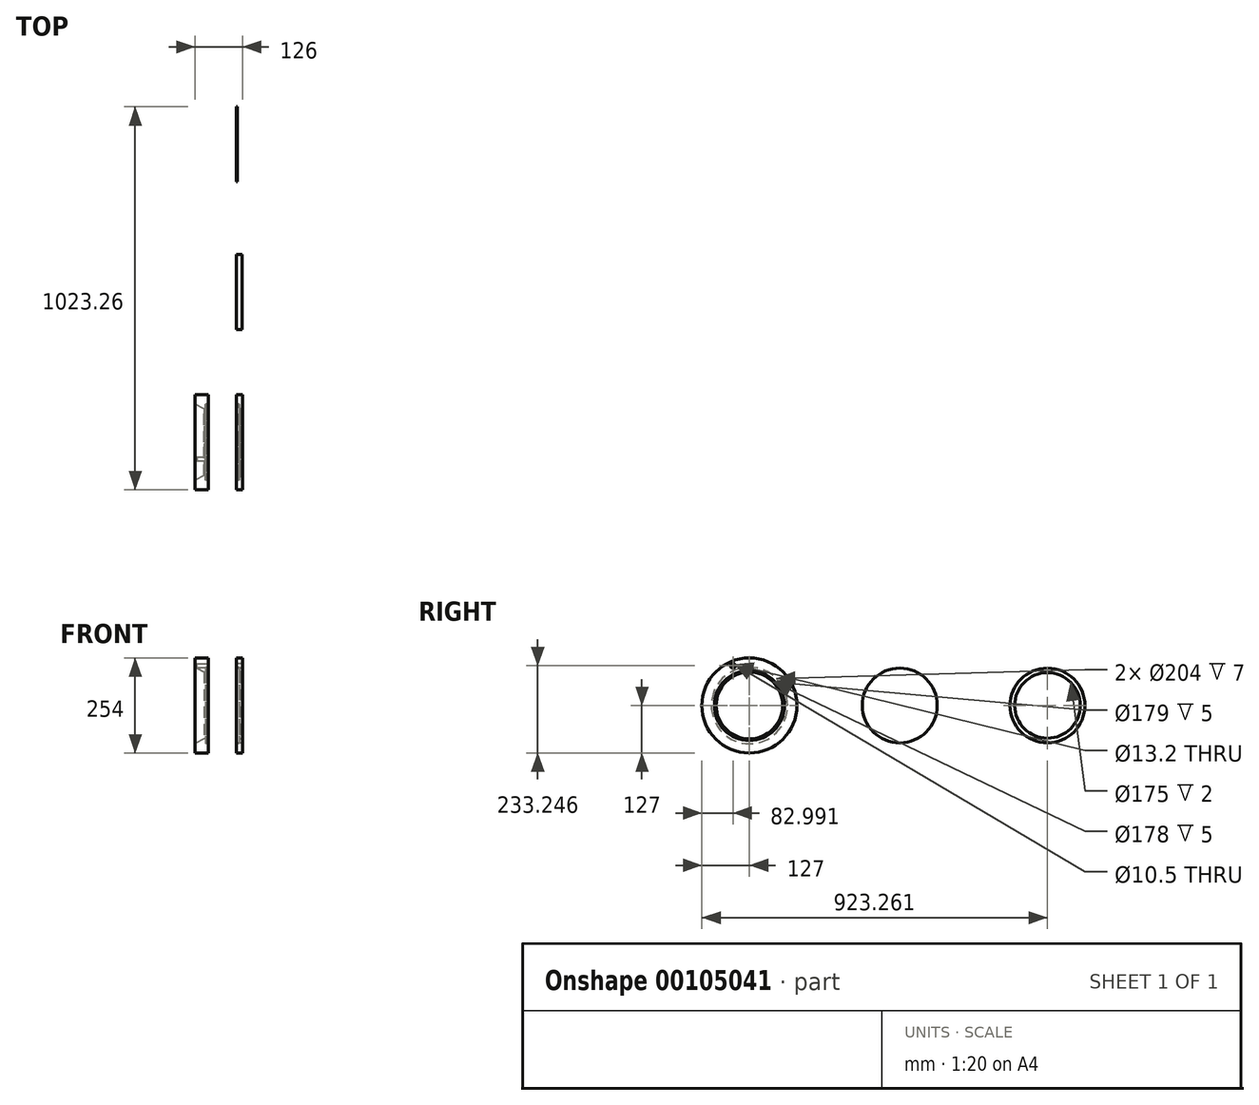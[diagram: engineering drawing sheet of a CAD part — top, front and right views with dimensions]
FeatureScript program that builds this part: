
annotation { "Feature Type Name" : "Feature", "Feature Type Description" : "" }
export const myFeature = defineFeature(function(context is Context, id is Id, definition is map)
    precondition{}
    {
        {
            var Q0;
            Q0=qCreatedBy(makeId("Front.planeOp"),FACE);
            var sketch = newSketch(context, id + "F0", { "sketchPlane" : qUnion([Q0])});
            skLineSegment(sketch, "E0", {"start": v(-110, 0) * mm, "end": v(0, 0) * mm, "construction": true});
            skLineSegment(sketch, "E1", {"start": v(0, 0) * mm, "end": v(162.86, 0) * mm, "construction": true});
            skPoint(sketch, "E2", {"position": v(0, 102) * mm});
            skPoint(sketch, "E3", {"position": v(7, 102) * mm});
            skPoint(sketch, "E4", {"position": v(7, 89.5) * mm});
            skPoint(sketch, "E5", {"position": v(16, 127) * mm});
            skPoint(sketch, "E6", {"position": v(0, 127) * mm});
            skLineSegment(sketch, "E7", {"start": v(0, 127) * mm, "end": v(16, 127) * mm});
            skLineSegment(sketch, "E8", {"start": v(16, 127) * mm, "end": v(16, 93.5) * mm});
            skLineSegment(sketch, "E9", {"start": v(7, 89.5) * mm, "end": v(12, 89.5) * mm});
            skLineSegment(sketch, "E10", {"start": v(7, 89.5) * mm, "end": v(7, 102) * mm});
            skLineSegment(sketch, "E11", {"start": v(7, 102) * mm, "end": v(0, 102) * mm});
            skLineSegment(sketch, "E12", {"start": v(0, 127) * mm, "end": v(0, 102) * mm});
            skLineSegment(sketch, "E13", {"start": v(12, 89.5) * mm, "end": v(16, 93.5) * mm});
            skPoint(sketch, "E14", {"position": v(-110, 127) * mm});
            skPoint(sketch, "E15", {"position": v(-75, 127) * mm});
            skPoint(sketch, "E16", {"position": v(-75, 102) * mm});
            skPoint(sketch, "E17", {"position": v(-82, 102) * mm});
            skPoint(sketch, "E18", {"position": v(-82, 89) * mm});
            skPoint(sketch, "E19", {"position": v(-87, 89) * mm});
            skPoint(sketch, "E20", {"position": v(-110, 102) * mm});
            skLineSegment(sketch, "E21", {"start": v(-110, 102) * mm, "end": v(-110, 127) * mm});
            skLineSegment(sketch, "E22", {"start": v(-110, 127) * mm, "end": v(-75, 127) * mm});
            skLineSegment(sketch, "E23", {"start": v(-75, 127) * mm, "end": v(-75, 102) * mm});
            skLineSegment(sketch, "E24", {"start": v(-75, 102) * mm, "end": v(-82, 102) * mm});
            skLineSegment(sketch, "E25", {"start": v(-82, 102) * mm, "end": v(-82, 89) * mm});
            skLineSegment(sketch, "E26", {"start": v(-82, 89) * mm, "end": v(-87, 89) * mm});
            skLineSegment(sketch, "E27", {"start": v(-87, 89) * mm, "end": v(-110, 102) * mm});
            skSolve(sketch);
        }
        {
            var Q0;
            Q0=makeQuery(id+"F0.imprint","IMPRINT",FACE,{"disambiguationData":[TD([[makeQuery(id+"F0.imprint","IMPRINT",EDGE,{"derivedFrom":sQuery(id+"F0.wireOp",EDGE,"E21")}),-1.0]])]});
            var Q1;
            Q1=sQuery(id+"F0.wireOp",EDGE,"E0");
            revolve(context, id + "F1", {"entities" : qUnion([Q0]), "axis" : qUnion([Q1]), "revolveType" : RevolveType.FULL});
        }
        {
            var Q0;
            Q0=makeQuery(id+"F0.imprint","IMPRINT",FACE,{"disambiguationData":[TD([[makeQuery(id+"F0.imprint","IMPRINT",EDGE,{"derivedFrom":sQuery(id+"F0.wireOp",EDGE,"E7")}),-1.0]])]});
            var Q1;
            Q1=sQuery(id+"F0.wireOp",EDGE,"E1");
            revolve(context, id + "F2", {"entities" : qUnion([Q0]), "axis" : qUnion([Q1]), "revolveType" : RevolveType.FULL});
        }
        {
            var Q0;
            Q0=makeQuery(id+"F2.opRevolve","SWEPT_FACE",FACE,{"disambiguationData":[OSD([sQuery(id+"F0.wireOp",EDGE,"E8")])]});
            var sketch = newSketch(context, id + "F3", { "sketchPlane" : qUnion([Q0])});
            skCircle(sketch, "E28", {"center": v(0, 0) * mm, "radius": 115 * mm, "construction": true});
            skLineSegment(sketch, "E29", {"start": v(0, 0) * mm, "end": v(-44, 106.25) * mm, "construction": true});
            skPoint(sketch, "E30", {"position": v(-44, 106.25) * mm});
            skSolve(sketch);
        }
        {
            var Q0;
            Q0=sQuery(id+"F3.wireOp",VERTEX,"E30");
            var Q1;
            Q1=makeQuery(id+"F2.opRevolve","SWEPT_BODY",BODY,{"disambiguationData":[OSD([sQuery(id+"F0.wireOp",EDGE,"E7"),sQuery(id+"F0.wireOp",EDGE,"E8"),sQuery(id+"F0.wireOp",EDGE,"E9"),sQuery(id+"F0.wireOp",EDGE,"E10"),sQuery(id+"F0.wireOp",EDGE,"E11"),sQuery(id+"F0.wireOp",EDGE,"E12"),sQuery(id+"F0.wireOp",EDGE,"E13")])]});
            hole(context, id + "F4", {"style" : HoleStyle.SIMPLE, "endStyle" : HoleEndStyle.THROUGH, "standardTappedOrClearance" : lookupTablePath({ "standard" : "ISO", "fit" : "Normal", "size" : "M12", "type" : "Clearance" }), "standardBlindInLast" : lookupTablePath({ "fit" : "Standard", "standard" : "ISO", "size" : "M12", "type" : "Clearance" }), "holeDiameter" : 13.2 * mm, "startFromSketch" : true, "locations" : qUnion([Q0]), "scope" : qUnion([Q1]), "isTappedThrough" : true});
        }
        {
            var Q0;
            Q0=makeQuery(id+"F1.opRevolve","SWEPT_FACE",FACE,{"disambiguationData":[OSD([sQuery(id+"F0.wireOp",EDGE,"E23")])]});
            var sketch = newSketch(context, id + "F5", { "sketchPlane" : qUnion([Q0])});
            skCircle(sketch, "E31", {"center": v(0, 0) * mm, "radius": 115 * mm, "construction": true});
            skLineSegment(sketch, "E32", {"start": v(0, 0) * mm, "end": v(-44, 106.25) * mm, "construction": true});
            skPoint(sketch, "E33", {"position": v(-44, 106.25) * mm});
            skSolve(sketch);
        }
        {
            var Q0;
            Q0=sQuery(id+"F5.wireOp",VERTEX,"E33");
            var Q1;
            Q1=makeQuery(id+"F1.opRevolve","SWEPT_BODY",BODY,{"disambiguationData":[OSD([sQuery(id+"F0.wireOp",EDGE,"E21"),sQuery(id+"F0.wireOp",EDGE,"E22"),sQuery(id+"F0.wireOp",EDGE,"E23"),sQuery(id+"F0.wireOp",EDGE,"E24"),sQuery(id+"F0.wireOp",EDGE,"E25"),sQuery(id+"F0.wireOp",EDGE,"E26"),sQuery(id+"F0.wireOp",EDGE,"E27")])]});
            hole(context, id + "F6", {"style" : HoleStyle.SIMPLE, "endStyle" : HoleEndStyle.BLIND, "standardTappedOrClearance" : lookupTablePath({ "standard" : "ISO", "engagement" : "75%", "pitch" : "1.5 mm", "size" : "M12", "type" : "Tapped" }), "standardBlindInLast" : lookupTablePath({ "standard" : "ISO", "engagement" : "75%", "pitch" : "1.5 mm", "size" : "M12", "type" : "Tapped" }), "holeDiameter" : 10.5 * mm, "holeDepth" : 30 * mm, "startFromSketch" : true, "locations" : qUnion([Q0]), "scope" : qUnion([Q1]), "majorDiameter" : 12 * mm});
        }
        {
            var Q0;
            Q0=qCreatedBy(makeId("Right.planeOp"),FACE);
            var sketch = newSketch(context, id + "F7", { "sketchPlane" : qUnion([Q0])});
            skCircle(sketch, "E34", {"center": v(401.83, 0) * mm, "radius": 100 * mm});
            skCircle(sketch, "E35", {"center": v(796.26, 0) * mm, "radius": 100 * mm});
            skCircle(sketch, "E36", {"center": v(796.26, 0) * mm, "radius": 87.5 * mm});
            skSolve(sketch);
        }
        {
            var Q0;
            Q0=makeQuery(id+"F7.imprint","IMPRINT",FACE,{"disambiguationData":[TD([[makeQuery(id+"F7.imprint","IMPRINT",EDGE,{"derivedFrom":sQuery(id+"F7.wireOp",EDGE,"E34")}),1.0]])]});
            extrude(context, id + "F8", {"entities" : qUnion([Q0]), "depth" : 15 * mm});
        }
        {
            var Q0;
            Q0=makeQuery(id+"F7.imprint","IMPRINT",FACE,{"disambiguationData":[TD([[makeQuery(id+"F7.imprint","IMPRINT",EDGE,{"derivedFrom":sQuery(id+"F7.wireOp",EDGE,"E35")}),1.0]])]});
            extrude(context, id + "F9", {"entities" : qUnion([Q0]), "depth" : 2 * mm});
        }
    });
